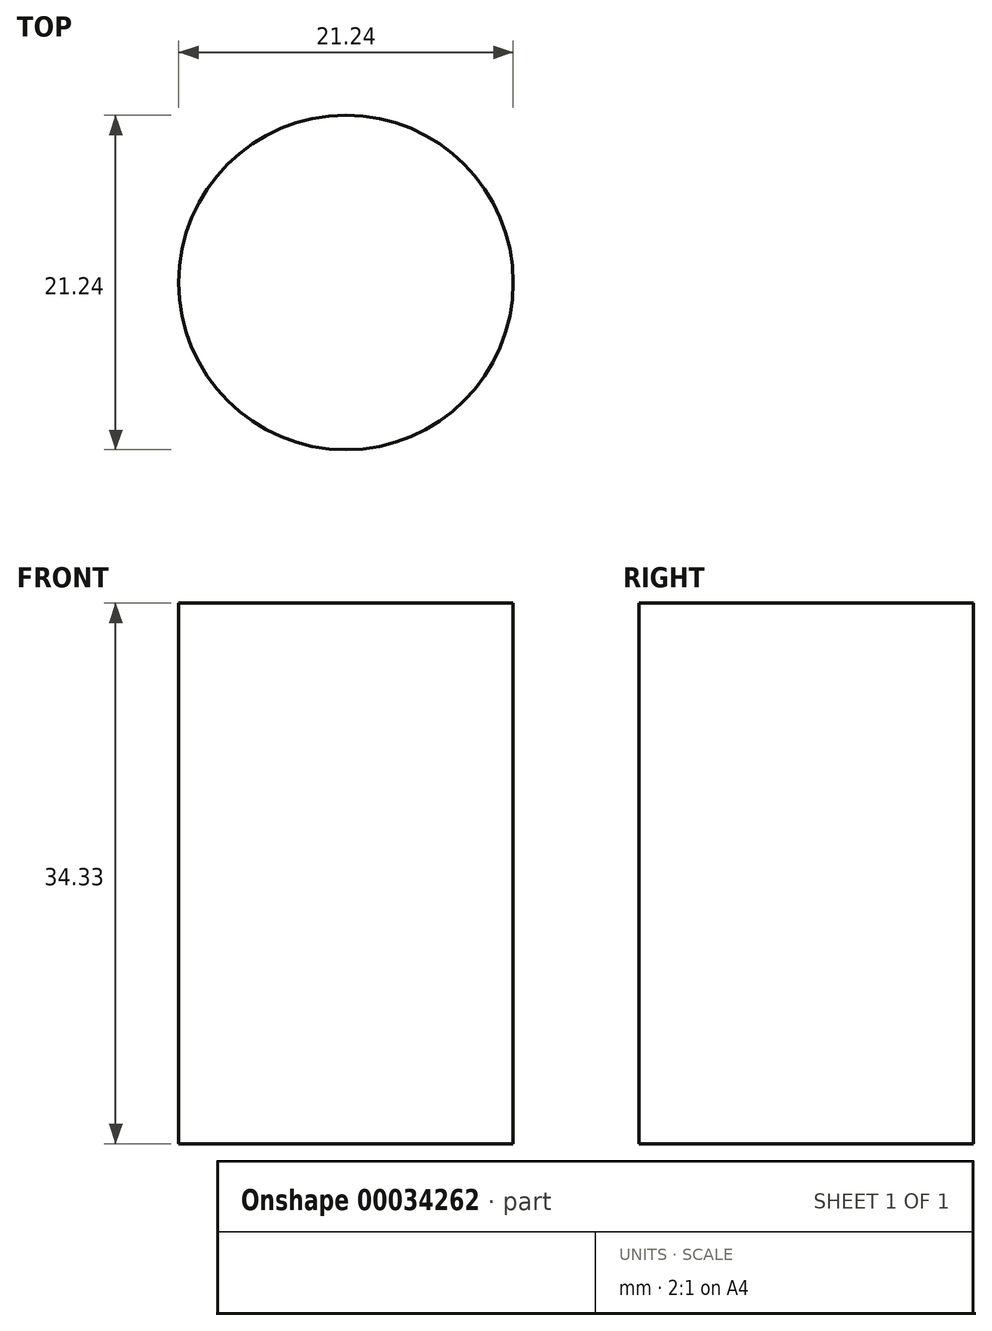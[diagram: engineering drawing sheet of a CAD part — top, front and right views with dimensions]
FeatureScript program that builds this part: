
annotation { "Feature Type Name" : "Feature", "Feature Type Description" : "" }
export const myFeature = defineFeature(function(context is Context, id is Id, definition is map)
    precondition{}
    {
        {
            var Q0;
            Q0=qCreatedBy(makeId("Top.planeOp"),FACE);
            var sketch = newSketch(context, id + "F0", { "sketchPlane" : qUnion([Q0])});
            skCircle(sketch, "E0", {"center": v(0, 0) * mm, "radius": 10.62 * mm});
            skSolve(sketch);
        }
        {
            var Q0;
            Q0 = qSketchRegion(id + "F0", true);
            extrude(context, id + "F1", {"entities" : qUnion([Q0]), "depth" : 34.33 * mm});
        }
    });
